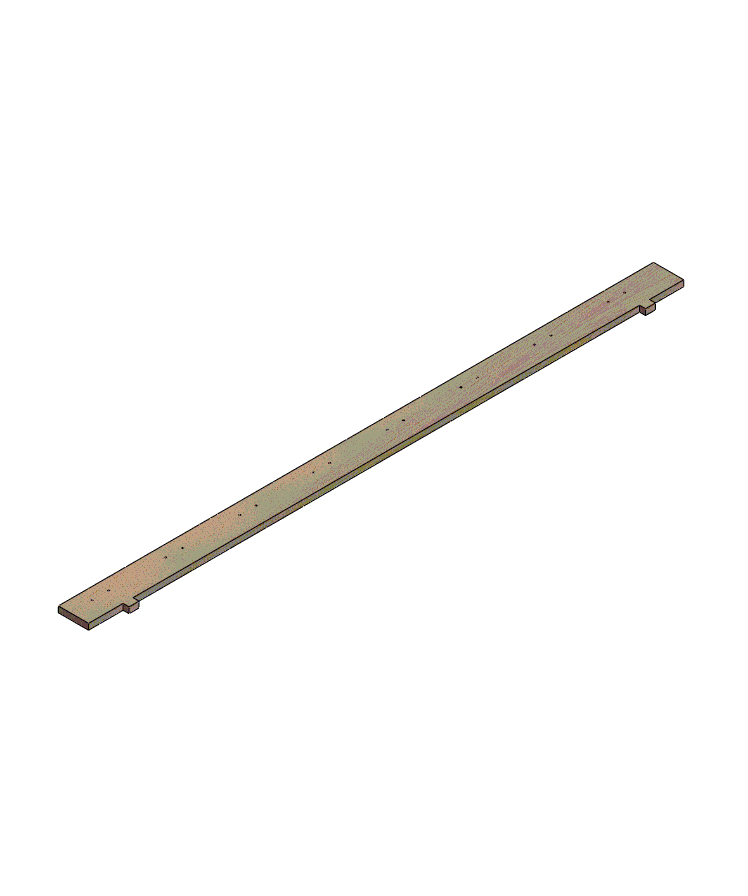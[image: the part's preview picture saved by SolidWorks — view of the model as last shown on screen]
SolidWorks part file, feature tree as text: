
SOLIDWORKS PART (.sldprt)
format: sldprt  version: not decoded by parser v0  size: 214,016 bytes
history: native  units: mm
features: sketch x3, extrude x2, material x1, cut_extrude x1 (+11 scaffold rows collapsed)
feature tree (18):
  scaffold x11  (default folders/planes/origin — collapsed)
  material  "Material <not specified>"
  sketch  "Sketch1"  dims[D1=1200.0mm D2=61.0mm]
  extrude  "Boss-Extrude1"  Depth=12mm
  sketch  "Sketch2"  dims[c1.D1=2.5mm c1.D2=2.5mm c2.D2=8.0]
  cut_extrude  "Cut-Extrude1"  Depth=20mm
  sketch  "Sketch3"  dims[D1=12.0mm D2=20.0mm D3=69.7mm D4=2.0]
  extrude  "Boss-Extrude2"  Depth=12mm
decode coverage: 6 of 6 modeling features carry decoded parameters
note: suppression state not decoded; provenance and decode notes live in map.json
